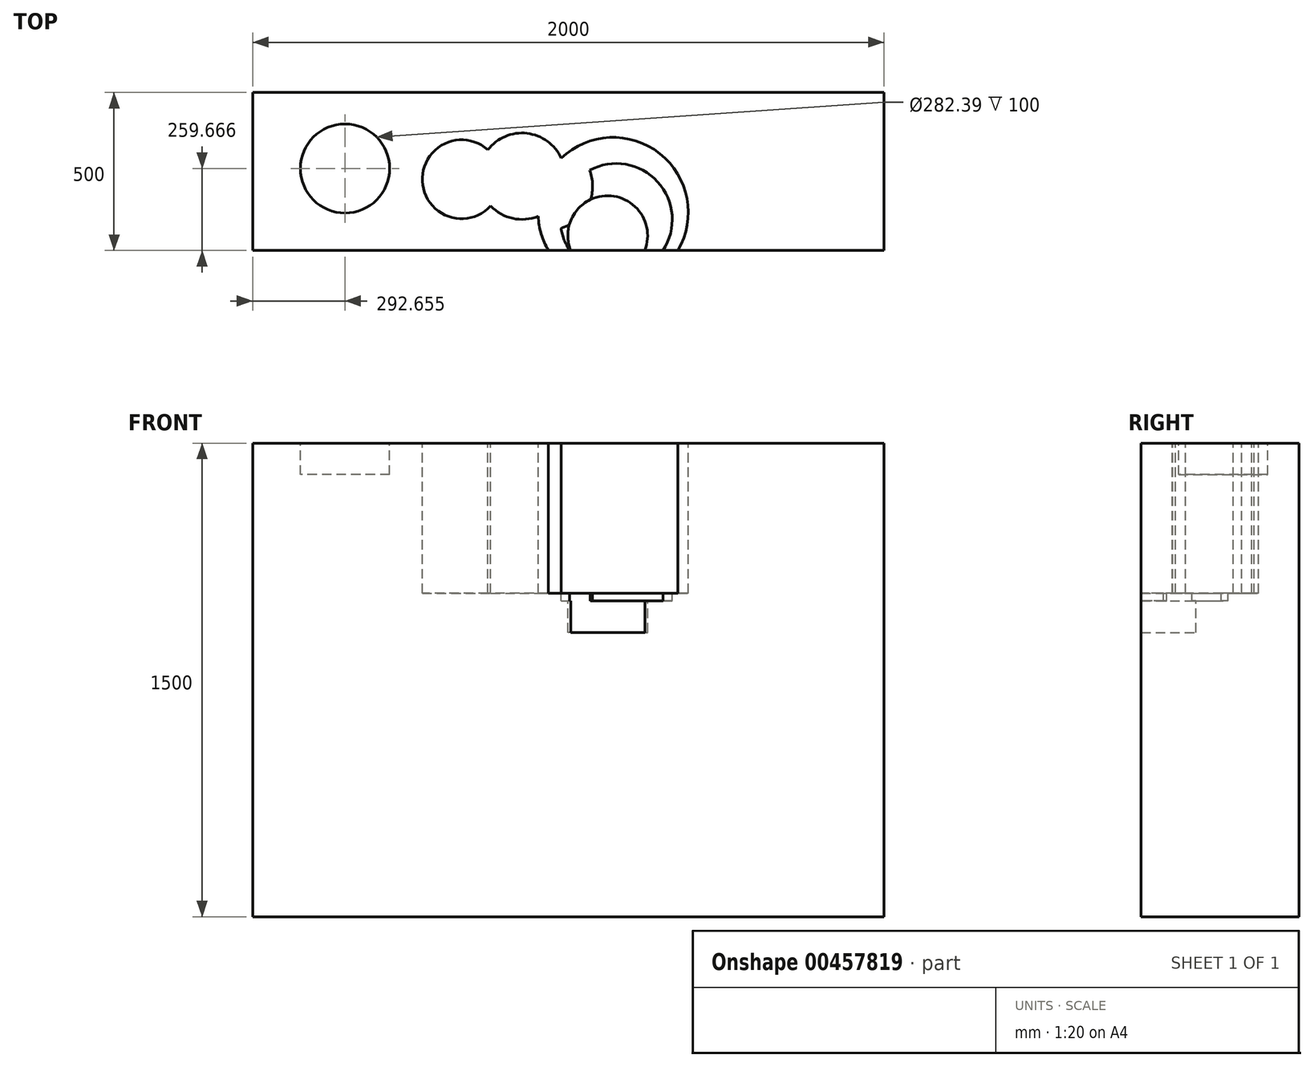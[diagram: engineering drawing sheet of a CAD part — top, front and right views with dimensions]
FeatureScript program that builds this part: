
annotation { "Feature Type Name" : "Feature", "Feature Type Description" : "" }
export const myFeature = defineFeature(function(context is Context, id is Id, definition is map)
    precondition{}
    {
        {
            var Q0;
            Q0=qCreatedBy(makeId("Top.planeOp"),FACE);
            var sketch = newSketch(context, id + "F0", { "sketchPlane" : qUnion([Q0])});
            skLineSegment(sketch, "E0.bottom", {"start": v(-1090.51, -284.54) * mm, "end": v(909.49, -284.54) * mm});
            skLineSegment(sketch, "E0.top", {"start": v(-1090.51, -784.54) * mm, "end": v(909.49, -784.54) * mm});
            skLineSegment(sketch, "E0.left", {"start": v(-1090.51, -284.54) * mm, "end": v(-1090.51, -784.54) * mm});
            skLineSegment(sketch, "E0.right", {"start": v(909.49, -284.54) * mm, "end": v(909.49, -784.54) * mm});
            skSolve(sketch);
        }
        {
            var Q0;
            Q0 = qSketchRegion(id + "F0", true);
            extrude(context, id + "F1", {"entities" : qUnion([Q0]), "oppositeDirection" : true, "depth" : 1500 * mm});
        }
        {
            var Q0;
            Q0=qCreatedBy(makeId("Top.planeOp"),FACE);
            var sketch = newSketch(context, id + "F2", { "sketchPlane" : qUnion([Q0])});
            skCircle(sketch, "E1", {"center": v(-797.85, -524.87) * mm, "radius": 141.2 * mm});
            skSolve(sketch);
        }
        {
            var Q0;
            Q0=makeQuery(id+"F2.imprint","IMPRINT",FACE,{"disambiguationData":[TD([[makeQuery(id+"F2.imprint","IMPRINT",EDGE,{"derivedFrom":sQuery(id+"F2.wireOp",EDGE,"E1")}),1.0]])]});
            extrude(context, id + "F3", {"entities" : qUnion([Q0]), "operationType" : NewBodyOperationType.REMOVE, "oppositeDirection" : true, "depth" : 100 * mm});
        }
        {
            var Q0;
            Q0=makeQuery(id+"F3.boolean.opBoolean","COPY",FACE,{"derivedFrom":makeQuery(id+"F3.opExtrude","CAP_FACE",FACE,{"disambiguationData":[OSD([sQuery(id+"F2.wireOp",EDGE,"E1")])],"isStart":false})});
            var sketch = newSketch(context, id + "F4", { "sketchPlane" : qUnion([Q0])});
            skCircle(sketch, "E2", {"center": v(-826.49, -472.62) * mm, "radius": 34.4 * mm});
            skCircle(sketch, "E3", {"center": v(-823.77, -586.84) * mm, "radius": 37 * mm});
            skSolve(sketch);
        }
        {
            var Q0;
            Q0=makeQuery(id+"F4.imprint","IMPRINT",FACE,{"disambiguationData":[TD([[makeQuery(id+"F4.imprint","IMPRINT",EDGE,{"derivedFrom":sQuery(id+"F4.wireOp",EDGE,"E2")}),1.0]])]});
            var Q1;
            Q1=makeQuery(id+"F1.opExtrude","CAP_FACE",FACE,{"disambiguationData":[OSD([sQuery(id+"F0.wireOp",EDGE,"E0.bottom"),sQuery(id+"F0.wireOp",EDGE,"E0.top"),sQuery(id+"F0.wireOp",EDGE,"E0.left"),sQuery(id+"F0.wireOp",EDGE,"E0.right")])],"isStart":true});
            extrude(context, id + "F5", {"entities" : qUnion([Q0, Q1]), "operationType" : NewBodyOperationType.REMOVE, "depth" : 300 * mm});
        }
        {
            var Q0;
            Q0=qCreatedBy(makeId("Top.planeOp"),FACE);
            var sketch = newSketch(context, id + "F6", { "sketchPlane" : qUnion([Q0])});
            skCircle(sketch, "E4", {"center": v(-837.37, -527.34) * mm, "radius": 22.26 * mm});
            skSolve(sketch);
        }
        {
            var Q0;
            Q0 = qSketchRegion(id + "F6", true);
            extrude(context, id + "F7", {"entities" : qUnion([Q0]), "operationType" : NewBodyOperationType.REMOVE, "oppositeDirection" : true, "depth" : 25 * mm});
        }
        {
            var Q0;
            Q0=qCreatedBy(makeId("Top.planeOp"),FACE);
            var sketch = newSketch(context, id + "F8", { "sketchPlane" : qUnion([Q0])});
            skCircle(sketch, "E5", {"center": v(-474.78, -424.52) * mm, "radius": 97.07 * mm});
            skCircle(sketch, "E6", {"center": v(-332.82, -478.37) * mm, "radius": 100.92 * mm});
            skCircle(sketch, "E7", {"center": v(-151.7, -581.17) * mm, "radius": 138.04 * mm});
            skCircle(sketch, "E8", {"center": v(61.24, -686.41) * mm, "radius": 177.2 * mm});
            skSolve(sketch);
        }
        {
            var Q0;
            {var subQ0=sQuery(id+"F8.wireOp",EDGE,"E8");var subQ1=sQuery(id+"F8.wireOp",EDGE,"E7");var subQ2=makeQuery(id+"F8.imprint","INTERSECT",VERTEX,{"disambiguationData":[OD(0.0)],"derivedFrom":[subQ1,subQ0]});Q0=makeQuery(id+"F8.imprint","IMPRINT",FACE,{"disambiguationData":[TD([[makeQuery(id+"F8.imprint","IMPRINT",EDGE,{"disambiguationData":[TD([[subQ2,1.0]])],"derivedFrom":subQ1}),-1.0]])]});}
            extrude(context, id + "F9", {"entities" : qUnion([Q0]), "operationType" : NewBodyOperationType.REMOVE, "oppositeDirection" : true, "depth" : 500 * mm});
        }
        {
            var Q0;
            Q0=qCreatedBy(makeId("Top.planeOp"),FACE);
            var sketch = newSketch(context, id + "F10", { "sketchPlane" : qUnion([Q0])});
            skCircle(sketch, "E9", {"center": v(-428.27, -559.14) * mm, "radius": 124.92 * mm});
            skCircle(sketch, "E10", {"center": v(-237.37, -549.35) * mm, "radius": 136.73 * mm});
            skCircle(sketch, "E11", {"center": v(51.45, -664.38) * mm, "radius": 237.87 * mm});
            skSolve(sketch);
        }
        {
            var Q0;
            Q0 = qSketchRegion(id + "F10", true);
            extrude(context, id + "F11", {"entities" : qUnion([Q0]), "operationType" : NewBodyOperationType.ADD, "depth" : 25 * mm});
        }
        {
            var Q0;
            Q0=makeQuery(id+"F11.opExtrude","CAP_FACE",FACE,{"disambiguationData":[OSD([sQuery(id+"F10.wireOp",EDGE,"E9"),sQuery(id+"F10.wireOp",EDGE,"E10"),sQuery(id+"F10.wireOp",EDGE,"E11")])],"isStart":false});
            extrude(context, id + "F12", {"entities" : qUnion([Q0]), "operationType" : NewBodyOperationType.REMOVE, "oppositeDirection" : true, "depth" : 500 * mm});
        }
        {
            var Q0;
            Q0=qCreatedBy(makeId("Top.planeOp"),FACE);
            var sketch = newSketch(context, id + "F13", { "sketchPlane" : qUnion([Q0])});
            skCircle(sketch, "E12", {"center": v(34.16, -737.56) * mm, "radius": 126.4 * mm});
            skSolve(sketch);
        }
        {
            var Q0;
            Q0 = qSketchRegion(id + "F13", true);
            extrude(context, id + "F14", {"entities" : qUnion([Q0]), "operationType" : NewBodyOperationType.REMOVE, "oppositeDirection" : true, "depth" : 600 * mm});
        }
    });
